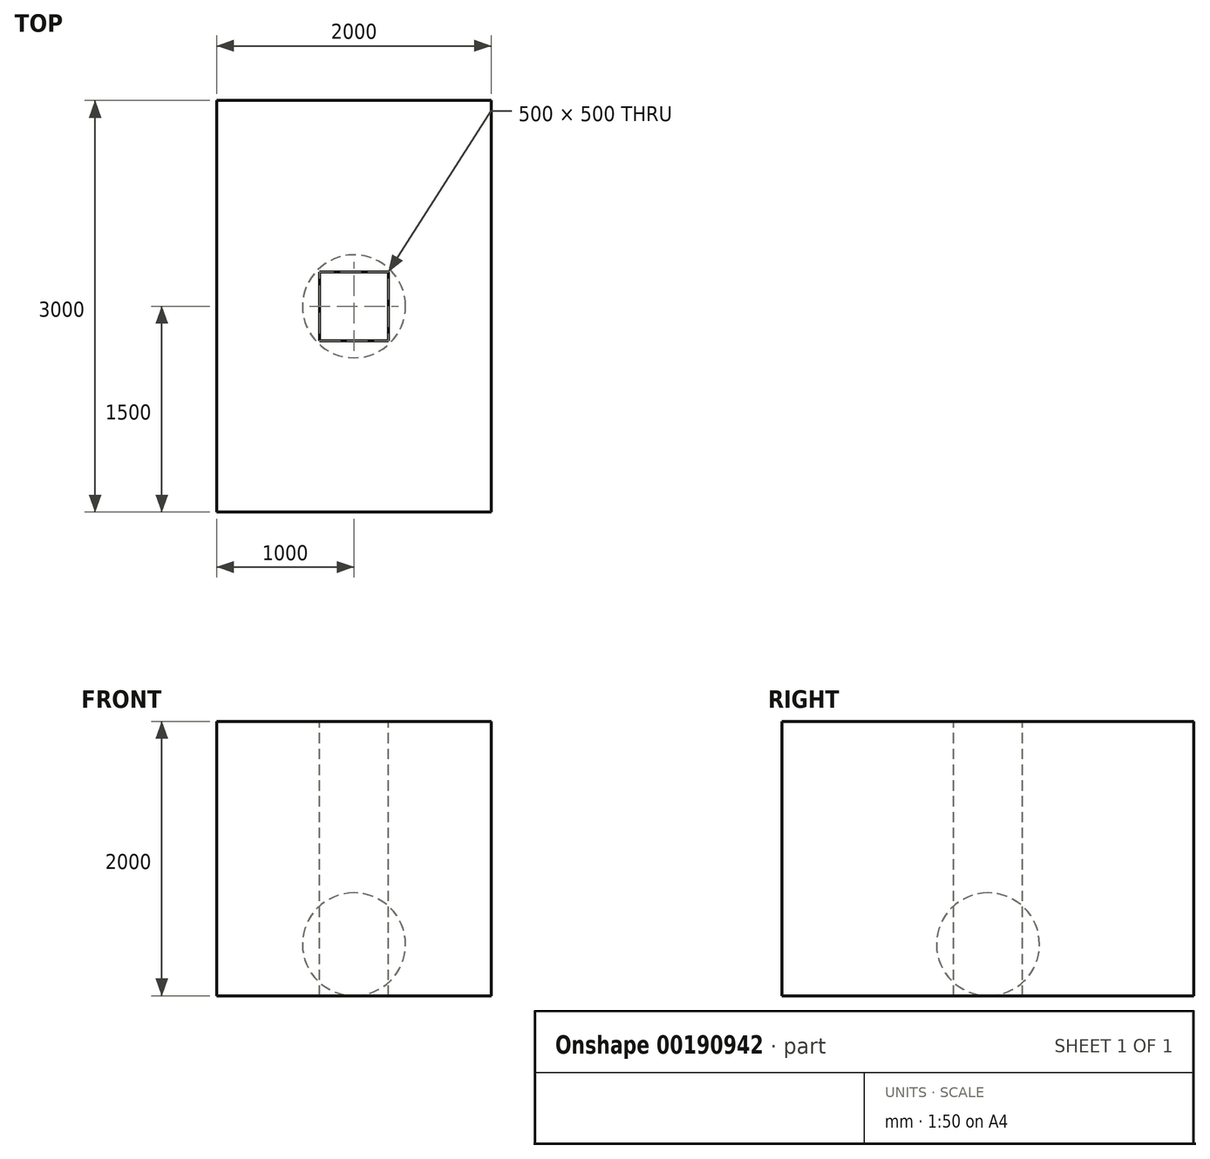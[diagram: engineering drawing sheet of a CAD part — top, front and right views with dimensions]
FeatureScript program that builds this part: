
annotation { "Feature Type Name" : "Feature", "Feature Type Description" : "" }
export const myFeature = defineFeature(function(context is Context, id is Id, definition is map)
    precondition{}
    {
        {
            var Q0;
            Q0=qCreatedBy(makeId("Front.planeOp"),FACE);
            var sketch = newSketch(context, id + "F0", { "sketchPlane" : qUnion([Q0])});
            skLineSegment(sketch, "E0.bottom", {"start": v(1000, 1000) * mm, "end": v(-1000, 1000) * mm});
            skLineSegment(sketch, "E0.top", {"start": v(1000, -1000) * mm, "end": v(-1000, -1000) * mm});
            skLineSegment(sketch, "E0.left", {"start": v(1000, 1000) * mm, "end": v(1000, -1000) * mm});
            skLineSegment(sketch, "E0.right", {"start": v(-1000, 1000) * mm, "end": v(-1000, -1000) * mm});
            skPoint(sketch, "E0.middle", {"position": v(0, 0) * mm});
            skSolve(sketch);
        }
        {
            var Q0;
            Q0 = qSketchRegion(id + "F0", true);
            extrude(context, id + "F1", {"entities" : qUnion([Q0]), "depth" : 3000 * mm, "offsetDistance" : 25 * mm, "symmetric" : true});
        }
        {
            var Q0;
            Q0=makeQuery(id+"F1.opExtrude","SWEPT_FACE",FACE,{"disambiguationData":[OSD([sQuery(id+"F0.wireOp",EDGE,"E0.bottom")])]});
            var sketch = newSketch(context, id + "F2", { "sketchPlane" : qUnion([Q0])});
            skLineSegment(sketch, "E1.bottom", {"start": v(250, 250) * mm, "end": v(-250, 250) * mm});
            skLineSegment(sketch, "E1.top", {"start": v(250, -250) * mm, "end": v(-250, -250) * mm});
            skLineSegment(sketch, "E1.left", {"start": v(250, 250) * mm, "end": v(250, -250) * mm});
            skLineSegment(sketch, "E1.right", {"start": v(-250, 250) * mm, "end": v(-250, -250) * mm});
            skPoint(sketch, "E1.middle", {"position": v(0, 0) * mm});
            skSolve(sketch);
        }
        {
            var Q0;
            Q0 = qSketchRegion(id + "F2", true);
            extrude(context, id + "F3", {"entities" : qUnion([Q0]), "operationType" : NewBodyOperationType.REMOVE, "endBound" : BoundingType.UP_TO_NEXT, "oppositeDirection" : true, "depth" : 25 * mm, "offsetDistance" : 25 * mm});
        }
        {
            var Q0;
            Q0=qCreatedBy(makeId("Front.planeOp"),FACE);
            var sketch = newSketch(context, id + "F4", { "sketchPlane" : qUnion([Q0])});
            skArc(sketch, "E2", {"start": v(0, -250) * mm, "mid": v(-375, -625) * mm, "end": v(0, -1000) * mm});
            skLineSegment(sketch, "E3", {"start": v(0, -1000) * mm, "end": v(0, -250) * mm});
            skSolve(sketch);
        }
        {
            var Q0;
            Q0=makeQuery(id+"F4.imprint","IMPRINT",FACE,{"disambiguationData":[TD([[makeQuery(id+"F4.imprint","IMPRINT",EDGE,{"derivedFrom":sQuery(id+"F4.wireOp",EDGE,"E2")}),1.0]])]});
            var Q1;
            Q1=sQuery(id+"F4.wireOp",EDGE,"E3");
            var Q2;
            Q2=sQuery(id+"F4.wireOp",EDGE,"E3");
            revolve(context, id + "F5", {"entities" : qUnion([Q0]), "surfaceEntities" : qUnion([Q1]), "axis" : qUnion([Q2]), "revolveType" : RevolveType.FULL});
        }
    });
